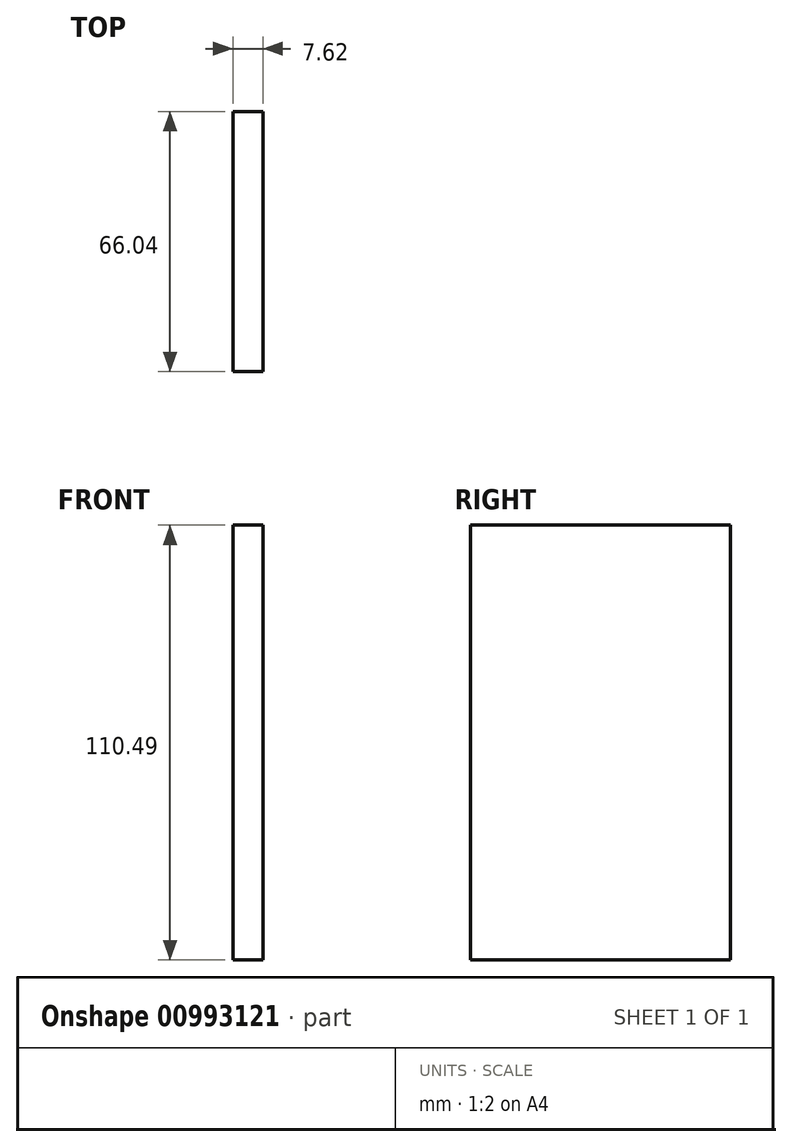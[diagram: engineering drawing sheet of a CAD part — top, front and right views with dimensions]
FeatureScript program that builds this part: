
annotation { "Feature Type Name" : "Feature", "Feature Type Description" : "" }
export const myFeature = defineFeature(function(context is Context, id is Id, definition is map)
    precondition{}
    {
        {
            var Q0;
            Q0=qCreatedBy(makeId("Right.planeOp"),FACE);
            var sketch = newSketch(context, id + "F0", { "sketchPlane" : qUnion([Q0])});
            skLineSegment(sketch, "E0.bottom", {"start": v(-56.5, 55.96) * mm, "end": v(9.55, 55.96) * mm});
            skLineSegment(sketch, "E0.top", {"start": v(-56.5, -54.53) * mm, "end": v(9.55, -54.53) * mm});
            skLineSegment(sketch, "E0.left", {"start": v(-56.5, 55.96) * mm, "end": v(-56.5, -54.53) * mm});
            skLineSegment(sketch, "E0.right", {"start": v(9.55, 55.96) * mm, "end": v(9.55, -54.53) * mm});
            skSolve(sketch);
        }
        {
            var Q0;
            Q0=makeQuery(id+"F0.imprint","IMPRINT",FACE,{"disambiguationData":[TD([[makeQuery(id+"F0.imprint","IMPRINT",EDGE,{"derivedFrom":sQuery(id+"F0.wireOp",EDGE,"E0.bottom")}),-1.0]])]});
            extrude(context, id + "F1", {"entities" : qUnion([Q0]), "depth" : 7.62 * mm, "offsetDistance" : 25.4 * mm});
        }
    });
